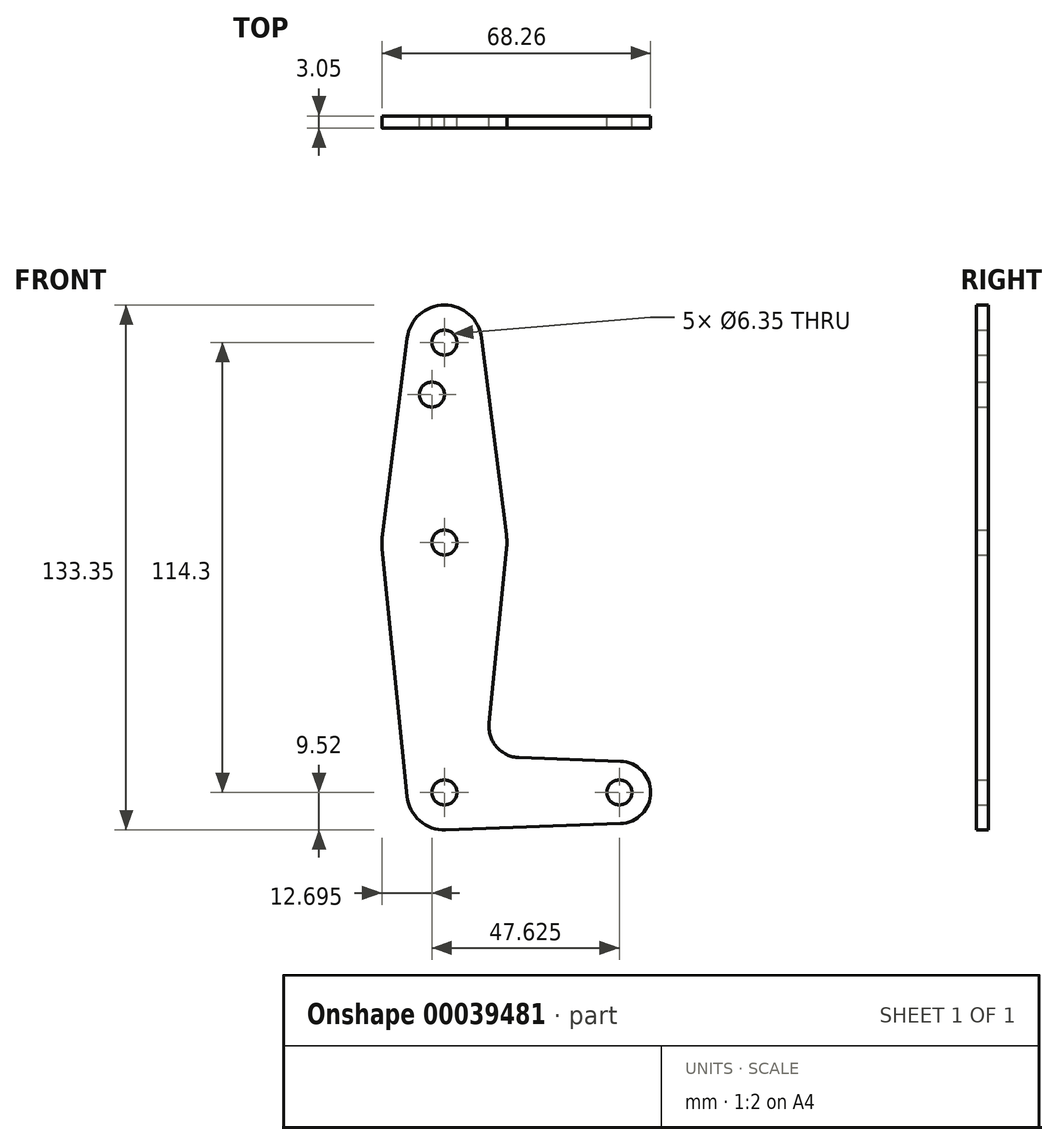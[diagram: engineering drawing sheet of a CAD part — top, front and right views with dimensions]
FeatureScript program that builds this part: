
annotation { "Feature Type Name" : "Feature", "Feature Type Description" : "" }
export const myFeature = defineFeature(function(context is Context, id is Id, definition is map)
    precondition{}
    {
        {
            var Q0;
            Q0=qCreatedBy(makeId("Front.planeOp"),FACE);
            var sketch = newSketch(context, id + "F0", { "sketchPlane" : qUnion([Q0])});
            skLineSegment(sketch, "E0", {"start": v(0, 0) * mm, "end": v(0, 114.3) * mm, "construction": true});
            skLineSegment(sketch, "E1", {"start": v(0, 0) * mm, "end": v(44.45, 0) * mm, "construction": true});
            skCircle(sketch, "E2", {"center": v(0, 114.3) * mm, "radius": 9.53 * mm});
            skCircle(sketch, "E3", {"center": v(0, 0) * mm, "radius": 9.53 * mm});
            skCircle(sketch, "E4", {"center": v(44.45, 0) * mm, "radius": 7.94 * mm});
            skCircle(sketch, "E5", {"center": v(0, 63.5) * mm, "radius": 15.88 * mm});
            skLineSegment(sketch, "E6", {"start": v(-9.45, 115.5) * mm, "end": v(-15.75, 65.48) * mm});
            skLineSegment(sketch, "E7", {"start": v(9.45, 115.5) * mm, "end": v(15.75, 65.48) * mm});
            skLineSegment(sketch, "E8", {"start": v(-15.8, 61.91) * mm, "end": v(-9.48, -0.95) * mm});
            skLineSegment(sketch, "E9", {"start": v(15.8, 61.91) * mm, "end": v(11.34, 17.6) * mm});
            skLineSegment(sketch, "E10", {"start": v(18.97, 8.85) * mm, "end": v(44.73, 7.93) * mm});
            skLineSegment(sketch, "E11", {"start": v(0.34, -9.52) * mm, "end": v(44.73, -7.93) * mm});
            skCircle(sketch, "E12", {"center": v(0, 114.3) * mm, "radius": 3.18 * mm});
            skCircle(sketch, "E13", {"center": v(-3.18, 101.1) * mm, "radius": 3.18 * mm});
            skCircle(sketch, "E14", {"center": v(0, 0) * mm, "radius": 3.18 * mm});
            skCircle(sketch, "E15", {"center": v(44.45, 0) * mm, "radius": 3.18 * mm});
            skArc(sketch, "E16.filletArc", {"start": v(11.34, 17.6) * mm, "mid": v(13.26, 11.57) * mm, "end": v(18.97, 8.85) * mm});
            skCircle(sketch, "E17", {"center": v(0, 63.5) * mm, "radius": 3.18 * mm});
            skSolve(sketch);
        }
        {
            var Q0;
            Q0 = qSketchRegion(id + "F0", true);
            extrude(context, id + "F1", {"entities" : qUnion([Q0]), "depth" : 3.05 * mm});
        }
    });
